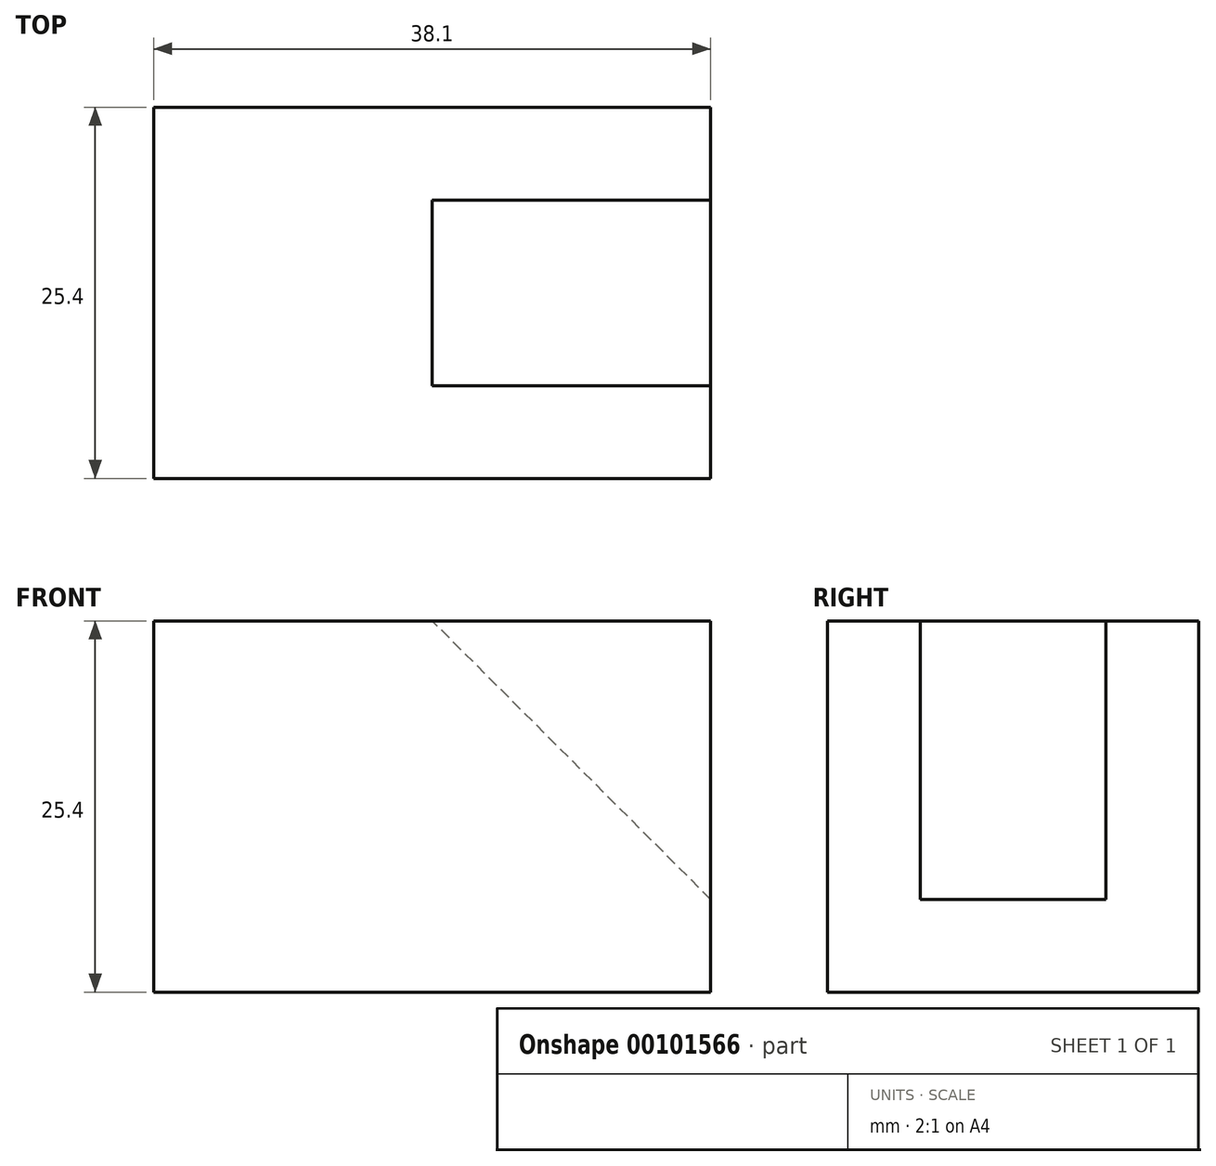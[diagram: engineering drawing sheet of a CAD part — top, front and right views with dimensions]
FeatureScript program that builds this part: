
annotation { "Feature Type Name" : "Feature", "Feature Type Description" : "" }
export const myFeature = defineFeature(function(context is Context, id is Id, definition is map)
    precondition{}
    {
        {
            var Q0;
            Q0=qCreatedBy(makeId("Front.planeOp"),FACE);
            var sketch = newSketch(context, id + "F0", { "sketchPlane" : qUnion([Q0])});
            skLineSegment(sketch, "E0.bottom", {"start": v(0, 0) * mm, "end": v(38.1, 0) * mm});
            skLineSegment(sketch, "E0.top", {"start": v(0, 25.4) * mm, "end": v(38.1, 25.4) * mm});
            skLineSegment(sketch, "E0.left", {"start": v(0, 0) * mm, "end": v(0, 25.4) * mm});
            skLineSegment(sketch, "E0.right", {"start": v(38.1, 0) * mm, "end": v(38.1, 25.4) * mm});
            skSolve(sketch);
        }
        {
            var Q0;
            Q0 = qSketchRegion(id + "F0", true);
            extrude(context, id + "F1", {"entities" : qUnion([Q0]), "endBound" : BoundingType.SYMMETRIC, "depth" : 25.4 * mm});
        }
        {
            var Q0;
            Q0=qCreatedBy(makeId("Front.planeOp"),FACE);
            var sketch = newSketch(context, id + "F2", { "sketchPlane" : qUnion([Q0])});
            skLineSegment(sketch, "E1", {"start": v(19.05, 25.4) * mm, "end": v(38.1, 25.4) * mm});
            skLineSegment(sketch, "E2", {"start": v(38.1, 25.4) * mm, "end": v(38.1, 6.35) * mm});
            skLineSegment(sketch, "E3", {"start": v(38.1, 6.35) * mm, "end": v(19.05, 25.4) * mm});
            skSolve(sketch);
        }
        {
            var Q0;
            Q0 = qSketchRegion(id + "F2", true);
            extrude(context, id + "F3", {"entities" : qUnion([Q0]), "operationType" : NewBodyOperationType.REMOVE, "endBound" : BoundingType.SYMMETRIC, "oppositeDirection" : true, "depth" : 12.7 * mm});
        }
    });
